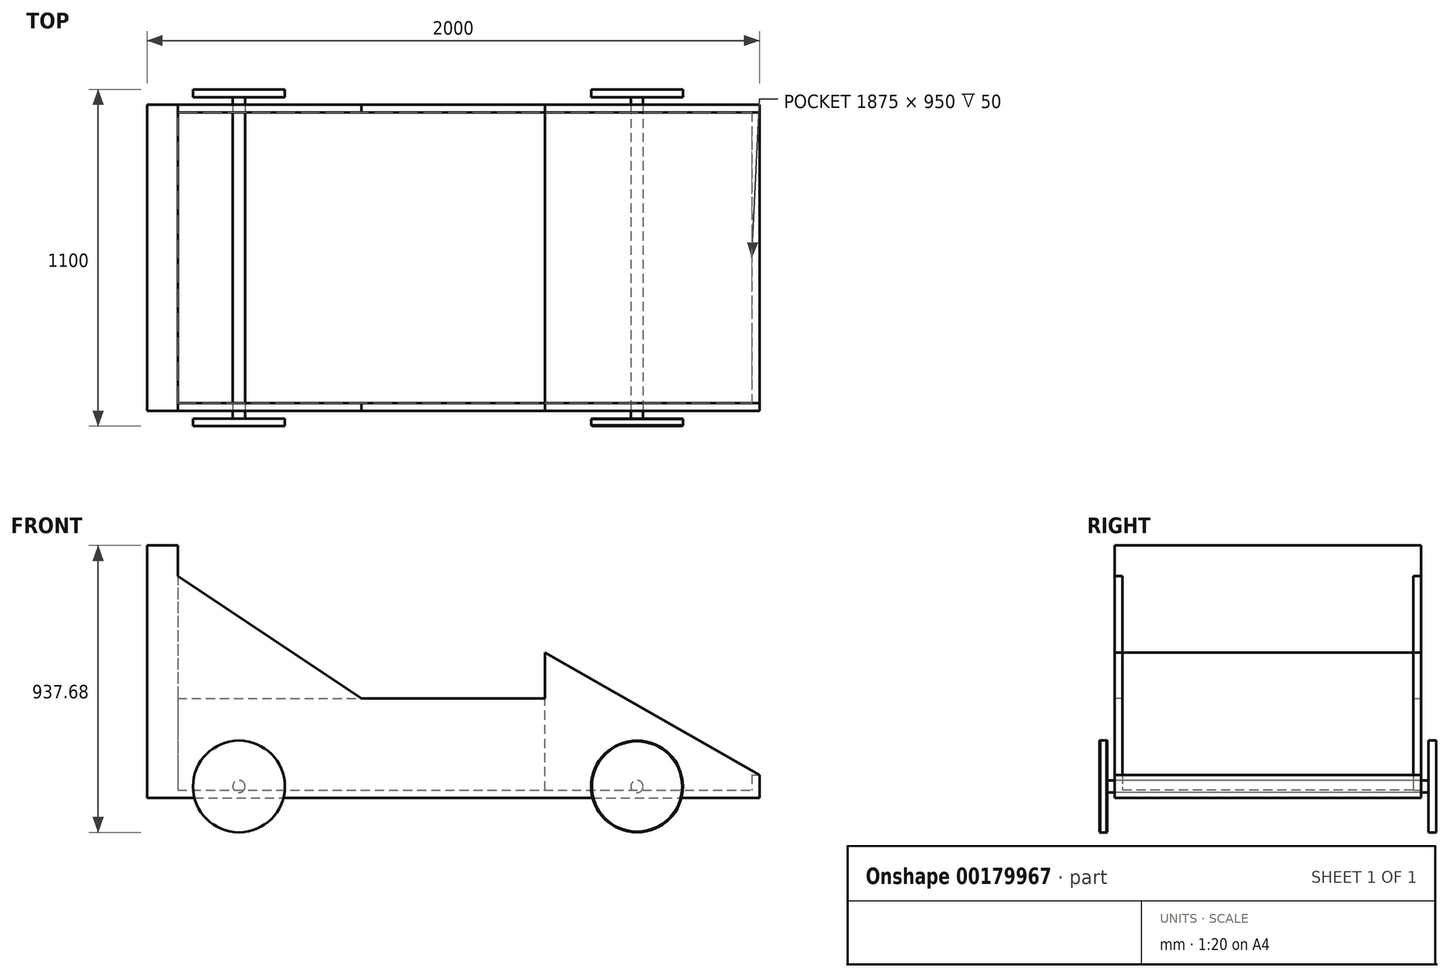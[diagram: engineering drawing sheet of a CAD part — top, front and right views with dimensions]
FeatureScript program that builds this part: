
annotation { "Feature Type Name" : "Feature", "Feature Type Description" : "" }
export const myFeature = defineFeature(function(context is Context, id is Id, definition is map)
    precondition{}
    {
        {
            var Q0;
            Q0=qCreatedBy(makeId("Top.planeOp"),FACE);
            var sketch = newSketch(context, id + "F0", { "sketchPlane" : qUnion([Q0])});
            skLineSegment(sketch, "E0.bottom", {"start": v(-1001.83, 499.3) * mm, "end": v(998.17, 499.3) * mm});
            skLineSegment(sketch, "E0.top", {"start": v(-1001.83, -500.7) * mm, "end": v(998.17, -500.7) * mm});
            skLineSegment(sketch, "E0.left", {"start": v(-1001.83, 499.3) * mm, "end": v(-1001.83, -500.7) * mm});
            skLineSegment(sketch, "E0.right", {"start": v(998.17, 499.3) * mm, "end": v(998.17, -500.7) * mm});
            skSolve(sketch);
        }
        {
            var Q0;
            Q0=makeQuery(id+"F0.imprint","IMPRINT",FACE,{"disambiguationData":[TD([[makeQuery(id+"F0.imprint","IMPRINT",EDGE,{"derivedFrom":sQuery(id+"F0.wireOp",EDGE,"E0.bottom")}),-1.0]])]});
            extrude(context, id + "F1", {"entities" : qUnion([Q0]), "depth" : 25 * mm});
        }
        {
            var Q0;
            Q0=makeQuery(id+"F1.opExtrude","CAP_FACE",FACE,{"disambiguationData":[OSD([sQuery(id+"F0.wireOp",EDGE,"E0.bottom"),sQuery(id+"F0.wireOp",EDGE,"E0.top"),sQuery(id+"F0.wireOp",EDGE,"E0.left"),sQuery(id+"F0.wireOp",EDGE,"E0.right")])],"isStart":false});
            var sketch = newSketch(context, id + "F2", { "sketchPlane" : qUnion([Q0])});
            skLineSegment(sketch, "E1.bottom", {"start": v(-1001.83, 499.3) * mm, "end": v(-901.83, 499.3) * mm});
            skLineSegment(sketch, "E1.top", {"start": v(-1001.83, -500.7) * mm, "end": v(-901.83, -500.7) * mm});
            skLineSegment(sketch, "E1.left", {"start": v(-1001.83, 499.3) * mm, "end": v(-1001.83, -500.7) * mm});
            skLineSegment(sketch, "E1.right", {"start": v(-901.83, 499.3) * mm, "end": v(-901.83, -500.7) * mm});
            skSolve(sketch);
        }
        {
            var Q0;
            Q0=makeQuery(id+"F2.imprint","IMPRINT",FACE,{"disambiguationData":[TD([[makeQuery(id+"F2.imprint","IMPRINT",EDGE,{"derivedFrom":sQuery(id+"F2.wireOp",EDGE,"E1.bottom")}),-1.0]])]});
            extrude(context, id + "F3", {"entities" : qUnion([Q0]), "operationType" : NewBodyOperationType.ADD, "depth" : 800 * mm});
        }
        {
            var Q0;
            Q0=makeQuery(id+"F1.opExtrude","CAP_FACE",FACE,{"disambiguationData":[OSD([sQuery(id+"F0.wireOp",EDGE,"E0.bottom"),sQuery(id+"F0.wireOp",EDGE,"E0.top"),sQuery(id+"F0.wireOp",EDGE,"E0.left"),sQuery(id+"F0.wireOp",EDGE,"E0.right")])],"isStart":false});
            var sketch = newSketch(context, id + "F4", { "sketchPlane" : qUnion([Q0])});
            skLineSegment(sketch, "E2.bottom", {"start": v(-901.83, -500.7) * mm, "end": v(298.17, -500.7) * mm});
            skLineSegment(sketch, "E2.top", {"start": v(-901.83, -475.7) * mm, "end": v(298.17, -475.7) * mm});
            skLineSegment(sketch, "E2.left", {"start": v(-901.83, -500.7) * mm, "end": v(-901.83, -475.7) * mm});
            skLineSegment(sketch, "E2.right", {"start": v(298.17, -500.7) * mm, "end": v(298.17, -475.7) * mm});
            skSolve(sketch);
        }
        {
            var Q0;
            Q0 = qSketchRegion(id + "F4", true);
            extrude(context, id + "F5", {"entities" : qUnion([Q0]), "operationType" : NewBodyOperationType.ADD, "depth" : 300 * mm});
        }
        {
            var Q0;
            Q0=makeQuery(id+"F5.boolean.opBoolean","MERGE",FACE,{"derivedFrom":[makeQuery(id+"F3.boolean.opBoolean","MERGE",FACE,{"derivedFrom":[makeQuery(id+"F1.opExtrude","SWEPT_FACE",FACE,{"disambiguationData":[OSD([sQuery(id+"F0.wireOp",EDGE,"E0.top")])]}),makeQuery(id+"F3.opExtrude","SWEPT_FACE",FACE,{"disambiguationData":[OSD([sQuery(id+"F2.wireOp",EDGE,"E1.top")])]})]}),makeQuery(id+"F5.opExtrude","SWEPT_FACE",FACE,{"disambiguationData":[OSD([sQuery(id+"F4.wireOp",EDGE,"E2.bottom")])]})]});
            var sketch = newSketch(context, id + "F6", { "sketchPlane" : qUnion([Q0])});
            skLineSegment(sketch, "E3", {"start": v(298.17, 25) * mm, "end": v(298.17, 475) * mm});
            skLineSegment(sketch, "E4", {"start": v(298.17, 475) * mm, "end": v(998.17, 75) * mm});
            skLineSegment(sketch, "E5", {"start": v(998.17, 75) * mm, "end": v(998.17, 25) * mm});
            skLineSegment(sketch, "E6", {"start": v(998.17, 25) * mm, "end": v(298.17, 25) * mm});
            skSolve(sketch);
        }
        {
            var Q0;
            {var subQ1=sQuery(id+"F6.wireOp",EDGE,"E4");Q0=makeQuery(id+"F6.imprint","IMPRINT",FACE,{"disambiguationData":[TD([[makeQuery(id+"F6.imprint","IMPRINT",EDGE,{"derivedFrom":subQ1}),-1.0]])]});}
            extrude(context, id + "F7", {"entities" : qUnion([Q0]), "operationType" : NewBodyOperationType.ADD, "oppositeDirection" : true, "depth" : 25 * mm});
        }
        {
            var Q0;
            Q0=makeQuery(id+"F3.boolean.opBoolean","MERGE",FACE,{"derivedFrom":[makeQuery(id+"F1.opExtrude","SWEPT_FACE",FACE,{"disambiguationData":[OSD([sQuery(id+"F0.wireOp",EDGE,"E0.bottom")])]}),makeQuery(id+"F3.opExtrude","SWEPT_FACE",FACE,{"disambiguationData":[OSD([sQuery(id+"F2.wireOp",EDGE,"E1.bottom")])]})]});
            var sketch = newSketch(context, id + "F8", { "sketchPlane" : qUnion([Q0])});
            skLineSegment(sketch, "E7.bottom", {"start": v(901.83, 25) * mm, "end": v(-298.17, 25) * mm});
            skLineSegment(sketch, "E7.top", {"start": v(901.83, 325) * mm, "end": v(-298.17, 325) * mm});
            skLineSegment(sketch, "E7.left", {"start": v(901.83, 25) * mm, "end": v(901.83, 325) * mm});
            skLineSegment(sketch, "E7.right", {"start": v(-298.17, 25) * mm, "end": v(-298.17, 325) * mm});
            skLineSegment(sketch, "E8", {"start": v(-298.17, 325) * mm, "end": v(-298.17, 475) * mm});
            skLineSegment(sketch, "E9", {"start": v(-298.17, 475) * mm, "end": v(-998.17, 75) * mm});
            skLineSegment(sketch, "E10", {"start": v(-998.17, 75) * mm, "end": v(-998.17, 25) * mm});
            skLineSegment(sketch, "E11", {"start": v(-998.17, 25) * mm, "end": v(-298.17, 25) * mm});
            skSolve(sketch);
        }
        {
            var Q0;
            Q0=makeQuery(id+"F8.imprint","IMPRINT",FACE,{"disambiguationData":[TD([[makeQuery(id+"F8.imprint","IMPRINT",EDGE,{"derivedFrom":sQuery(id+"F8.wireOp",EDGE,"E7.bottom")}),-1.0]])]});
            extrude(context, id + "F9", {"entities" : qUnion([Q0]), "oppositeDirection" : true, "depth" : 25 * mm});
        }
        {
            var Q0;
            Q0 = qSketchRegion(id + "F8", true);
            extrude(context, id + "F10", {"entities" : qUnion([Q0]), "oppositeDirection" : true, "depth" : 25 * mm});
        }
        {
            var Q0;
            Q0=makeQuery(id+"F7.boolean.opBoolean","MERGE",FACE,{"derivedFrom":[makeQuery(id+"F1.opExtrude","SWEPT_FACE",FACE,{"disambiguationData":[OSD([sQuery(id+"F0.wireOp",EDGE,"E0.right")])]}),makeQuery(id+"F7.opExtrude","SWEPT_FACE",FACE,{"disambiguationData":[OSD([sQuery(id+"F6.wireOp",EDGE,"E5")])]})]});
            var sketch = newSketch(context, id + "F11", { "sketchPlane" : qUnion([Q0])});
            skLineSegment(sketch, "E12.bottom", {"start": v(-500.7, 0) * mm, "end": v(499.3, 0) * mm});
            skLineSegment(sketch, "E12.top", {"start": v(-500.7, 75) * mm, "end": v(499.3, 75) * mm});
            skLineSegment(sketch, "E12.left", {"start": v(-500.7, 0) * mm, "end": v(-500.7, 75) * mm});
            skLineSegment(sketch, "E12.right", {"start": v(499.3, 0) * mm, "end": v(499.3, 75) * mm});
            skSolve(sketch);
        }
        {
            var Q0;
            {var subQ1=makeQuery(id+"F7.opExtrude","CAP_EDGE",EDGE,{"disambiguationData":[OSD([sQuery(id+"F6.wireOp",EDGE,"E5")])],"isStart":false});Q0=makeQuery(id+"F11.imprint","IMPRINT",FACE,{"disambiguationData":[TD([[makeQuery(id+"F11.imprint","IMPRINT",EDGE,{"derivedFrom":subQ1}),1.0]])]});}
            extrude(context, id + "F12", {"entities" : qUnion([Q0]), "operationType" : NewBodyOperationType.ADD, "oppositeDirection" : true, "depth" : 25 * mm});
        }
        {
            var Q0;
            Q0=makeQuery(id+"F7.opExtrude","SWEPT_FACE",FACE,{"disambiguationData":[OSD([sQuery(id+"F6.wireOp",EDGE,"E4")])]});
            var sketch = newSketch(context, id + "F13", { "sketchPlane" : qUnion([Q0])});
            skLineSegment(sketch, "E13.bottom", {"start": v(23.22, -475.7) * mm, "end": v(829.45, -475.7) * mm});
            skLineSegment(sketch, "E13.top", {"start": v(23.22, 474.3) * mm, "end": v(829.45, 474.3) * mm});
            skLineSegment(sketch, "E13.left", {"start": v(23.22, -475.7) * mm, "end": v(23.22, 474.3) * mm});
            skLineSegment(sketch, "E13.right", {"start": v(829.45, -475.7) * mm, "end": v(829.45, 474.3) * mm});
            skSolve(sketch);
        }
        {
            var Q0;
            Q0=makeQuery(id+"F13.imprint","IMPRINT",FACE,{"disambiguationData":[TD([[makeQuery(id+"F13.imprint","IMPRINT",EDGE,{"derivedFrom":sQuery(id+"F13.wireOp",EDGE,"E13.bottom")}),1.0]])]});
            extrude(context, id + "F14", {"entities" : qUnion([Q0]), "oppositeDirection" : true, "depth" : 1 * mm});
        }
        {
            var Q0;
            Q0=makeQuery(id+"F7.boolean.opBoolean","MERGE",FACE,{"derivedFrom":[makeQuery(id+"F5.boolean.opBoolean","MERGE",FACE,{"derivedFrom":[makeQuery(id+"F3.boolean.opBoolean","MERGE",FACE,{"derivedFrom":[makeQuery(id+"F1.opExtrude","SWEPT_FACE",FACE,{"disambiguationData":[OSD([sQuery(id+"F0.wireOp",EDGE,"E0.top")])]}),makeQuery(id+"F3.opExtrude","SWEPT_FACE",FACE,{"disambiguationData":[OSD([sQuery(id+"F2.wireOp",EDGE,"E1.top")])]})]}),makeQuery(id+"F5.opExtrude","SWEPT_FACE",FACE,{"disambiguationData":[OSD([sQuery(id+"F4.wireOp",EDGE,"E2.bottom")])]})]}),makeQuery(id+"F7.opExtrude","CAP_FACE",FACE,{"disambiguationData":[OSD([sQuery(id+"F6.wireOp",EDGE,"E3"),sQuery(id+"F6.wireOp",EDGE,"E4"),sQuery(id+"F6.wireOp",EDGE,"E5"),sQuery(id+"F6.wireOp",EDGE,"E6")])],"isStart":true})]});
            var sketch = newSketch(context, id + "F15", { "sketchPlane" : qUnion([Q0])});
            skLineSegment(sketch, "E14", {"start": v(-301.83, 325) * mm, "end": v(-901.83, 725) * mm});
            skLineSegment(sketch, "E15", {"start": v(-901.83, 725) * mm, "end": v(-901.83, 325) * mm});
            skLineSegment(sketch, "E16", {"start": v(-901.83, 325) * mm, "end": v(-301.83, 325) * mm});
            skSolve(sketch);
        }
        {
            var Q0;
            Q0 = qSketchRegion(id + "F15", true);
            extrude(context, id + "F16", {"entities" : qUnion([Q0]), "operationType" : NewBodyOperationType.ADD, "oppositeDirection" : true, "depth" : 25 * mm});
        }
        {
            var Q0;
            Q0=makeQuery(id+"F10.opExtrude","CAP_FACE",FACE,{"disambiguationData":[OSD([sQuery(id+"F8.wireOp",EDGE,"E7.bottom"),sQuery(id+"F8.wireOp",EDGE,"E7.top"),sQuery(id+"F8.wireOp",EDGE,"E7.left"),sQuery(id+"F8.wireOp",EDGE,"E8"),sQuery(id+"F8.wireOp",EDGE,"E9"),sQuery(id+"F8.wireOp",EDGE,"E10"),sQuery(id+"F8.wireOp",EDGE,"E11")])],"isStart":true});
            var sketch = newSketch(context, id + "F17", { "sketchPlane" : qUnion([Q0])});
            skLineSegment(sketch, "E17", {"start": v(301.83, 325) * mm, "end": v(901.83, 725) * mm});
            skLineSegment(sketch, "E18", {"start": v(901.83, 725) * mm, "end": v(901.83, 325) * mm});
            skLineSegment(sketch, "E19", {"start": v(901.83, 325) * mm, "end": v(301.83, 325) * mm});
            skSolve(sketch);
        }
        {
            var Q0;
            Q0=makeQuery(id+"F17.imprint","IMPRINT",FACE,{"disambiguationData":[TD([[makeQuery(id+"F17.imprint","IMPRINT",EDGE,{"derivedFrom":sQuery(id+"F17.wireOp",EDGE,"E17")}),-1.0]])]});
            extrude(context, id + "F18", {"entities" : qUnion([Q0]), "oppositeDirection" : true, "depth" : 25 * mm});
        }
        {
            var Q0;
            Q0=makeQuery(id+"F16.boolean.opBoolean","MERGE",FACE,{"derivedFrom":[makeQuery(id+"F7.boolean.opBoolean","MERGE",FACE,{"derivedFrom":[makeQuery(id+"F5.boolean.opBoolean","MERGE",FACE,{"derivedFrom":[makeQuery(id+"F3.boolean.opBoolean","MERGE",FACE,{"derivedFrom":[makeQuery(id+"F1.opExtrude","SWEPT_FACE",FACE,{"disambiguationData":[OSD([sQuery(id+"F0.wireOp",EDGE,"E0.top")])]}),makeQuery(id+"F3.opExtrude","SWEPT_FACE",FACE,{"disambiguationData":[OSD([sQuery(id+"F2.wireOp",EDGE,"E1.top")])]})]}),makeQuery(id+"F5.opExtrude","SWEPT_FACE",FACE,{"disambiguationData":[OSD([sQuery(id+"F4.wireOp",EDGE,"E2.bottom")])]})]}),makeQuery(id+"F7.opExtrude","CAP_FACE",FACE,{"disambiguationData":[OSD([sQuery(id+"F6.wireOp",EDGE,"E3"),sQuery(id+"F6.wireOp",EDGE,"E4"),sQuery(id+"F6.wireOp",EDGE,"E5"),sQuery(id+"F6.wireOp",EDGE,"E6")])],"isStart":true})]}),makeQuery(id+"F16.opExtrude","CAP_FACE",FACE,{"disambiguationData":[OSD([sQuery(id+"F15.wireOp",EDGE,"E14"),sQuery(id+"F15.wireOp",EDGE,"E15"),sQuery(id+"F15.wireOp",EDGE,"E16")])],"isStart":true})]});
            var sketch = newSketch(context, id + "F19", { "sketchPlane" : qUnion([Q0])});
            skCircle(sketch, "E20", {"center": v(598.17, 37.32) * mm, "radius": 20 * mm});
            skCircle(sketch, "E21", {"center": v(-701.83, 37.32) * mm, "radius": 20 * mm});
            skSolve(sketch);
        }
        {
            var Q0;
            Q0=makeQuery(id+"F19.imprint","IMPRINT",FACE,{"disambiguationData":[TD([[makeQuery(id+"F19.imprint","IMPRINT",EDGE,{"derivedFrom":sQuery(id+"F19.wireOp",EDGE,"E21")}),1.0]])]});
            var Q1;
            Q1=makeQuery(id+"F19.imprint","IMPRINT",FACE,{"disambiguationData":[TD([[makeQuery(id+"F19.imprint","IMPRINT",EDGE,{"derivedFrom":sQuery(id+"F19.wireOp",EDGE,"E20")}),1.0]])]});
            extrude(context, id + "F20", {"entities" : qUnion([Q0, Q1]), "oppositeDirection" : true, "depth" : 1025 * mm});
        }
        {
            var Q0;
            Q0=makeQuery(id+"F20.opExtrude","CAP_FACE",FACE,{"disambiguationData":[OSD([sQuery(id+"F19.wireOp",EDGE,"E21")])],"isStart":true});
            var Q1;
            Q1 = qSketchRegion(id + "F19", true);
            extrude(context, id + "F21", {"entities" : qUnion([Q0, Q1]), "depth" : 25 * mm});
        }
        {
            var Q0;
            {var subQ0=sQuery(id+"F19.wireOp",EDGE,"E21");Q0=makeQuery(id+"F21.opExtrude","CAP_FACE",FACE,{"disambiguationData":[OSD([subQ0]),TDD([makeQuery(id+"F19.imprint","IMPRINT",EDGE,{"derivedFrom":subQ0})])],"isStart":false});}
            var sketch = newSketch(context, id + "F22", { "sketchPlane" : qUnion([Q0])});
            skCircle(sketch, "E22", {"center": v(-701.83, 37.32) * mm, "radius": 150 * mm});
            skSolve(sketch);
        }
        {
            var Q0;
            Q0=makeQuery(id+"F21.opExtrude","CAP_FACE",FACE,{"disambiguationData":[OSD([sQuery(id+"F19.wireOp",EDGE,"E20")])],"isStart":false});
            var sketch = newSketch(context, id + "F23", { "sketchPlane" : qUnion([Q0])});
            skCircle(sketch, "E23", {"center": v(598.17, 37.32) * mm, "radius": 150 * mm});
            skSolve(sketch);
        }
        {
            var Q0;
            Q0=makeQuery(id+"F22.imprint","IMPRINT",FACE,{"disambiguationData":[TD([[makeQuery(id+"F22.imprint","IMPRINT",EDGE,{"derivedFrom":sQuery(id+"F22.wireOp",EDGE,"E22")}),1.0]])]});
            var Q1;
            Q1=makeQuery(id+"F23.imprint","IMPRINT",FACE,{"disambiguationData":[TD([[makeQuery(id+"F23.imprint","IMPRINT",EDGE,{"derivedFrom":sQuery(id+"F23.wireOp",EDGE,"E23")}),1.0]])]});
            var Q2;
            {var subQ0=sQuery(id+"F19.wireOp",EDGE,"E21");Q2=makeQuery(id+"F22.imprint","IMPRINT",FACE,{"disambiguationData":[TD([[makeQuery(id+"F22.imprint","IMPRINT",EDGE,{"derivedFrom":makeQuery(id+"F21.opExtrude","CAP_EDGE",EDGE,{"disambiguationData":[OSD([subQ0]),TDD([makeQuery(id+"F19.imprint","IMPRINT",EDGE,{"derivedFrom":subQ0})])],"isStart":false})}),1.0]])]});}
            var Q3;
            Q3=makeQuery(id+"F23.imprint","IMPRINT",FACE,{"disambiguationData":[TD([[makeQuery(id+"F23.imprint","IMPRINT",EDGE,{"derivedFrom":makeQuery(id+"F21.opExtrude","CAP_EDGE",EDGE,{"disambiguationData":[OSD([sQuery(id+"F19.wireOp",EDGE,"E20")])],"isStart":false})}),1.0]])]});
            extrude(context, id + "F24", {"entities" : qUnion([Q0, Q1, Q2, Q3]), "depth" : 25 * mm});
        }
        {
            var Q0;
            Q0=makeQuery(id+"F20.opExtrude","CAP_FACE",FACE,{"disambiguationData":[OSD([sQuery(id+"F19.wireOp",EDGE,"E20")])],"isStart":false});
            var sketch = newSketch(context, id + "F25", { "sketchPlane" : qUnion([Q0])});
            skCircle(sketch, "E24", {"center": v(-598.17, 37.32) * mm, "radius": 150 * mm});
            skSolve(sketch);
        }
        {
            var Q0;
            Q0=makeQuery(id+"F20.opExtrude","CAP_FACE",FACE,{"disambiguationData":[OSD([sQuery(id+"F19.wireOp",EDGE,"E21")])],"isStart":false});
            var sketch = newSketch(context, id + "F26", { "sketchPlane" : qUnion([Q0])});
            skCircle(sketch, "E25", {"center": v(701.83, 37.32) * mm, "radius": 150 * mm});
            skSolve(sketch);
        }
        {
            var Q0;
            Q0=makeQuery(id+"F25.imprint","IMPRINT",FACE,{"disambiguationData":[TD([[makeQuery(id+"F25.imprint","IMPRINT",EDGE,{"derivedFrom":sQuery(id+"F25.wireOp",EDGE,"E24")}),1.0]])]});
            var Q1;
            Q1=makeQuery(id+"F25.imprint","IMPRINT",FACE,{"disambiguationData":[TD([[makeQuery(id+"F25.imprint","IMPRINT",EDGE,{"derivedFrom":makeQuery(id+"F20.opExtrude","CAP_EDGE",EDGE,{"disambiguationData":[OSD([sQuery(id+"F19.wireOp",EDGE,"E20")])],"isStart":false})}),-1.0]])]});
            var Q2;
            Q2=makeQuery(id+"F26.imprint","IMPRINT",FACE,{"disambiguationData":[TD([[makeQuery(id+"F26.imprint","IMPRINT",EDGE,{"derivedFrom":sQuery(id+"F26.wireOp",EDGE,"E25")}),1.0]])]});
            var Q3;
            Q3=makeQuery(id+"F26.imprint","IMPRINT",FACE,{"disambiguationData":[TD([[makeQuery(id+"F26.imprint","IMPRINT",EDGE,{"derivedFrom":makeQuery(id+"F20.opExtrude","CAP_EDGE",EDGE,{"disambiguationData":[OSD([sQuery(id+"F19.wireOp",EDGE,"E21")])],"isStart":false})}),-1.0]])]});
            extrude(context, id + "F27", {"entities" : qUnion([Q0, Q1, Q2, Q3]), "depth" : 25 * mm});
        }
        {
            var Q0;
            Q0=makeQuery(id+"F24.opExtrude","CAP_EDGE",EDGE,{"disambiguationData":[OSD([sQuery(id+"F23.wireOp",EDGE,"E23")])],"isStart":false});
            var Q1;
            Q1=makeQuery(id+"F24.opExtrude","CAP_EDGE",EDGE,{"disambiguationData":[OSD([sQuery(id+"F23.wireOp",EDGE,"E23")])],"isStart":true});
            chamfer(context, id + "F28", {"entities" : qUnion([Q0, Q1]), "width" : 2.5 * mm, "tangentPropagation" : true});
        }
    });
